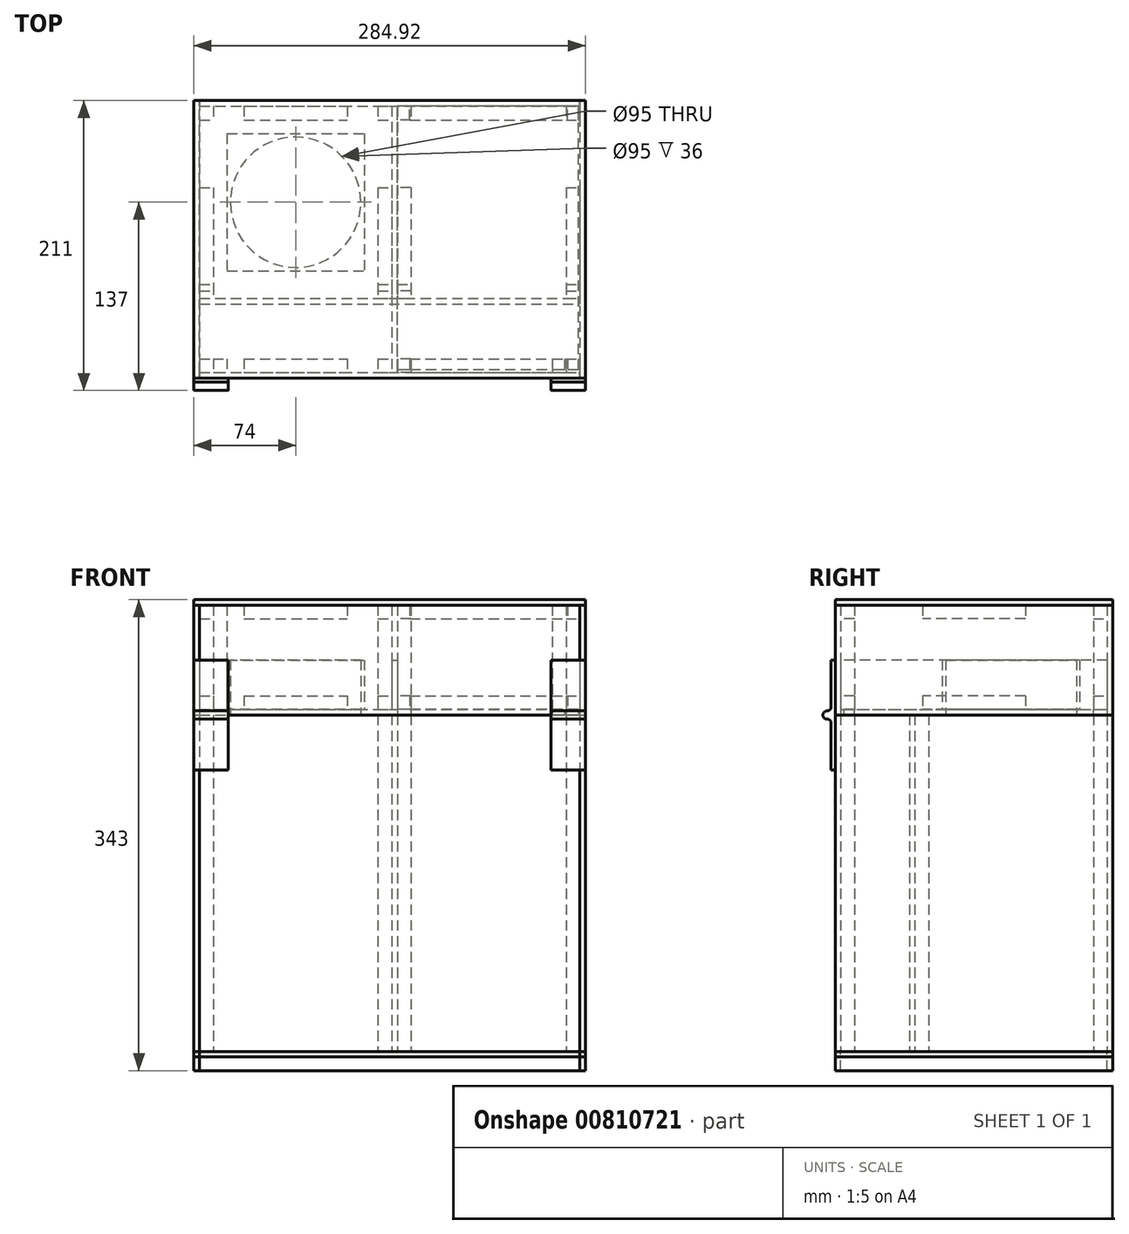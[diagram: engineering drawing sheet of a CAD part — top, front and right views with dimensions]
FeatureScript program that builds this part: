
annotation { "Feature Type Name" : "Feature", "Feature Type Description" : "" }
export const myFeature = defineFeature(function(context is Context, id is Id, definition is map)
    precondition{}
    {
        {
            assignVariable(context, id + "F0", {"name" : "Hoogte", "anyValue" : 245 * mm});
        }
        {
            assignVariable(context, id + "F1", {"name" : "Dikte", "anyValue" : 4 * mm});
        }
        {
            assignVariable(context, id + "F2", {"name" : "Hoogtedak", "anyValue" : 80 * mm});
        }
        {
            var Q0;
            Q0=qCreatedBy(makeId("Top.planeOp"),FACE);
            var sketch = newSketch(context, id + "F3", { "sketchPlane" : qUnion([Q0])});
            skPoint(sketch, "E0.second.point", {"position": v(-37.5, 0) * mm});
            skPoint(sketch, "E0.third.point", {"position": v(-144, 71.58) * mm});
            skLineSegment(sketch, "E1.bottom", {"start": v(132.92, 0) * mm, "end": v(-144, 0) * mm, "construction": true});
            skLineSegment(sketch, "E1.top", {"start": v(132.92, -4) * mm, "end": v(-144, -4) * mm, "construction": true});
            skLineSegment(sketch, "E1.left", {"start": v(132.92, 0) * mm, "end": v(132.92, -4) * mm, "construction": true});
            skLineSegment(sketch, "E1.right", {"start": v(-144, 0) * mm, "end": v(-144, -4) * mm, "construction": true});
            skCircle(sketch, "E2", {"center": v(40, 40) * mm, "radius": 40 * mm, "construction": true});
            skPoint(sketch, "E2.first.point", {"position": v(40, 0) * mm});
            skPoint(sketch, "E2.second.point", {"position": v(0, 40) * mm});
            skPoint(sketch, "E2.third.point", {"position": v(57.46, 76) * mm});
            skCircle(sketch, "E3", {"center": v(92.92, 100) * mm, "radius": 40 * mm, "construction": true});
            skPoint(sketch, "E3.first.point", {"position": v(66.46, 70) * mm});
            skPoint(sketch, "E3.second.point", {"position": v(132.92, 100) * mm});
            skPoint(sketch, "E3.third.point", {"position": v(61.07, 124.2) * mm});
            skLineSegment(sketch, "E4.bottom", {"start": v(0, 0) * mm, "end": v(-4, 0) * mm, "construction": true});
            skLineSegment(sketch, "E4.top", {"start": v(0, 140) * mm, "end": v(-4, 140) * mm, "construction": true});
            skLineSegment(sketch, "E4.left", {"start": v(0, 0) * mm, "end": v(0, 140) * mm, "construction": true});
            skLineSegment(sketch, "E4.right", {"start": v(-4, 0) * mm, "end": v(-4, 140) * mm, "construction": true});
            skCircle(sketch, "E5", {"center": v(-74, 70) * mm, "radius": 70 * mm, "construction": true});
            skPoint(sketch, "E5.first.point", {"position": v(-74, 0) * mm});
            skPoint(sketch, "E5.second.point", {"position": v(-4, 70) * mm});
            skPoint(sketch, "E5.third.point", {"position": v(-109.65, 130.24) * mm});
            skLineSegment(sketch, "E6.bottom", {"start": v(-144, -4) * mm, "end": v(132.92, -4) * mm, "construction": true});
            skLineSegment(sketch, "E6.top", {"start": v(-144, -54) * mm, "end": v(132.92, -54) * mm, "construction": true});
            skLineSegment(sketch, "E6.left", {"start": v(-144, -4) * mm, "end": v(-144, -54) * mm, "construction": true});
            skLineSegment(sketch, "E6.right", {"start": v(132.92, -4) * mm, "end": v(132.92, -54) * mm, "construction": true});
            skLineSegment(sketch, "E7.top", {"start": v(-144, 140) * mm, "end": v(132.92, 140) * mm, "construction": true});
            skLineSegment(sketch, "E7.left", {"start": v(-144, -54) * mm, "end": v(-144, 140) * mm, "construction": true});
            skLineSegment(sketch, "E7.right", {"start": v(132.92, -54) * mm, "end": v(132.92, 140) * mm, "construction": true});
            skLineSegment(sketch, "E8.bottom", {"start": v(132.92, 140) * mm, "end": v(122.92, 140) * mm, "construction": true});
            skLineSegment(sketch, "E8.top", {"start": v(132.92, 130) * mm, "end": v(122.92, 130) * mm, "construction": true});
            skLineSegment(sketch, "E8.left", {"start": v(132.92, 140) * mm, "end": v(132.92, 130) * mm, "construction": true});
            skLineSegment(sketch, "E8.right", {"start": v(122.92, 140) * mm, "end": v(122.92, 130) * mm, "construction": true});
            skLineSegment(sketch, "E9.bottom", {"start": v(0, 140) * mm, "end": v(10, 140) * mm, "construction": true});
            skLineSegment(sketch, "E9.top", {"start": v(0, 130) * mm, "end": v(10, 130) * mm, "construction": true});
            skLineSegment(sketch, "E9.left", {"start": v(0, 140) * mm, "end": v(0, 130) * mm, "construction": true});
            skLineSegment(sketch, "E9.right", {"start": v(10, 140) * mm, "end": v(10, 130) * mm, "construction": true});
            skLineSegment(sketch, "E10.bottom", {"start": v(-4, 140) * mm, "end": v(-14, 140) * mm, "construction": true});
            skLineSegment(sketch, "E10.top", {"start": v(-4, 130) * mm, "end": v(-14, 130) * mm, "construction": true});
            skLineSegment(sketch, "E10.left", {"start": v(-4, 140) * mm, "end": v(-4, 130) * mm, "construction": true});
            skLineSegment(sketch, "E10.right", {"start": v(-14, 140) * mm, "end": v(-14, 130) * mm, "construction": true});
            skLineSegment(sketch, "E11.bottom", {"start": v(-144, 140) * mm, "end": v(-134, 140) * mm, "construction": true});
            skLineSegment(sketch, "E11.top", {"start": v(-144, 130) * mm, "end": v(-134, 130) * mm, "construction": true});
            skLineSegment(sketch, "E11.left", {"start": v(-144, 140) * mm, "end": v(-144, 130) * mm, "construction": true});
            skLineSegment(sketch, "E11.right", {"start": v(-134, 140) * mm, "end": v(-134, 130) * mm, "construction": true});
            skLineSegment(sketch, "E12.bottom", {"start": v(-144, 0) * mm, "end": v(-134, 0) * mm, "construction": true});
            skLineSegment(sketch, "E12.top", {"start": v(-144, 10) * mm, "end": v(-134, 10) * mm, "construction": true});
            skLineSegment(sketch, "E12.left", {"start": v(-144, 0) * mm, "end": v(-144, 10) * mm, "construction": true});
            skLineSegment(sketch, "E12.right", {"start": v(-134, 0) * mm, "end": v(-134, 10) * mm, "construction": true});
            skLineSegment(sketch, "E13.bottom", {"start": v(-4, 0) * mm, "end": v(-14, 0) * mm, "construction": true});
            skLineSegment(sketch, "E13.top", {"start": v(-4, 10) * mm, "end": v(-14, 10) * mm, "construction": true});
            skLineSegment(sketch, "E13.left", {"start": v(-4, 0) * mm, "end": v(-4, 10) * mm, "construction": true});
            skLineSegment(sketch, "E13.right", {"start": v(-14, 0) * mm, "end": v(-14, 10) * mm, "construction": true});
            skLineSegment(sketch, "E14.bottom", {"start": v(0, 0) * mm, "end": v(10, 0) * mm, "construction": true});
            skLineSegment(sketch, "E14.top", {"start": v(0, 10) * mm, "end": v(10, 10) * mm, "construction": true});
            skLineSegment(sketch, "E14.left", {"start": v(0, 0) * mm, "end": v(0, 10) * mm, "construction": true});
            skLineSegment(sketch, "E14.right", {"start": v(10, 0) * mm, "end": v(10, 10) * mm, "construction": true});
            skLineSegment(sketch, "E15.bottom", {"start": v(132.92, 0) * mm, "end": v(122.92, 0) * mm, "construction": true});
            skLineSegment(sketch, "E15.top", {"start": v(132.92, 10) * mm, "end": v(122.92, 10) * mm, "construction": true});
            skLineSegment(sketch, "E15.left", {"start": v(132.92, 0) * mm, "end": v(132.92, 10) * mm, "construction": true});
            skLineSegment(sketch, "E15.right", {"start": v(122.92, 0) * mm, "end": v(122.92, 10) * mm, "construction": true});
            skLineSegment(sketch, "E16.bottom", {"start": v(132.92, -54) * mm, "end": v(122.92, -54) * mm, "construction": true});
            skLineSegment(sketch, "E16.top", {"start": v(132.92, -44) * mm, "end": v(122.92, -44) * mm, "construction": true});
            skLineSegment(sketch, "E16.left", {"start": v(132.92, -54) * mm, "end": v(132.92, -44) * mm, "construction": true});
            skLineSegment(sketch, "E16.right", {"start": v(122.92, -54) * mm, "end": v(122.92, -44) * mm, "construction": true});
            skLineSegment(sketch, "E17.bottom", {"start": v(-144, -54) * mm, "end": v(-134, -54) * mm, "construction": true});
            skLineSegment(sketch, "E17.top", {"start": v(-144, -44) * mm, "end": v(-134, -44) * mm, "construction": true});
            skLineSegment(sketch, "E17.left", {"start": v(-144, -54) * mm, "end": v(-144, -44) * mm, "construction": true});
            skLineSegment(sketch, "E17.right", {"start": v(-134, -54) * mm, "end": v(-134, -44) * mm, "construction": true});
            skSolve(sketch);
        }
        {
            var Q0;
            Q0=qCreatedBy(makeId("Top.planeOp"),FACE);
            var sketch = newSketch(context, id + "F4", { "sketchPlane" : qUnion([Q0])});
            skLineSegment(sketch, "E18.bottom", {"start": v(-144, 140) * mm, "end": v(-134, 140) * mm});
            skLineSegment(sketch, "E18.top", {"start": v(-144, 130) * mm, "end": v(-134, 130) * mm});
            skLineSegment(sketch, "E18.left", {"start": v(-144, 140) * mm, "end": v(-144, 130) * mm});
            skLineSegment(sketch, "E18.right", {"start": v(-134, 140) * mm, "end": v(-134, 130) * mm});
            skLineSegment(sketch, "E19.bottom", {"start": v(-14, 140) * mm, "end": v(-4, 140) * mm});
            skLineSegment(sketch, "E19.top", {"start": v(-14, 130) * mm, "end": v(-4, 130) * mm});
            skLineSegment(sketch, "E19.left", {"start": v(-14, 140) * mm, "end": v(-14, 130) * mm});
            skLineSegment(sketch, "E19.right", {"start": v(-4, 140) * mm, "end": v(-4, 130) * mm});
            skLineSegment(sketch, "E20.bottom", {"start": v(10, 140) * mm, "end": v(0, 140) * mm});
            skLineSegment(sketch, "E20.top", {"start": v(10, 130) * mm, "end": v(0, 130) * mm});
            skLineSegment(sketch, "E20.left", {"start": v(10, 140) * mm, "end": v(10, 130) * mm});
            skLineSegment(sketch, "E20.right", {"start": v(0, 140) * mm, "end": v(0, 130) * mm});
            skLineSegment(sketch, "E21.bottom", {"start": v(122.92, 140) * mm, "end": v(132.92, 140) * mm});
            skLineSegment(sketch, "E21.top", {"start": v(122.92, 130) * mm, "end": v(132.92, 130) * mm});
            skLineSegment(sketch, "E21.left", {"start": v(122.92, 140) * mm, "end": v(122.92, 130) * mm});
            skLineSegment(sketch, "E21.right", {"start": v(132.92, 140) * mm, "end": v(132.92, 130) * mm});
            skLineSegment(sketch, "E22.bottom", {"start": v(122.92, 10) * mm, "end": v(132.92, 10) * mm});
            skLineSegment(sketch, "E22.top", {"start": v(122.92, 0) * mm, "end": v(132.92, 0) * mm});
            skLineSegment(sketch, "E22.left", {"start": v(122.92, 10) * mm, "end": v(122.92, 0) * mm});
            skLineSegment(sketch, "E22.right", {"start": v(132.92, 10) * mm, "end": v(132.92, 0) * mm});
            skLineSegment(sketch, "E23.bottom", {"start": v(122.92, -44) * mm, "end": v(132.92, -44) * mm});
            skLineSegment(sketch, "E23.top", {"start": v(122.92, -54) * mm, "end": v(132.92, -54) * mm});
            skLineSegment(sketch, "E23.left", {"start": v(122.92, -44) * mm, "end": v(122.92, -54) * mm});
            skLineSegment(sketch, "E23.right", {"start": v(132.92, -44) * mm, "end": v(132.92, -54) * mm});
            skLineSegment(sketch, "E24.bottom", {"start": v(0, 10) * mm, "end": v(10, 10) * mm});
            skLineSegment(sketch, "E24.top", {"start": v(0, 0) * mm, "end": v(10, 0) * mm});
            skLineSegment(sketch, "E24.left", {"start": v(0, 10) * mm, "end": v(0, 0) * mm});
            skLineSegment(sketch, "E24.right", {"start": v(10, 10) * mm, "end": v(10, 0) * mm});
            skLineSegment(sketch, "E25.bottom", {"start": v(-14, 10) * mm, "end": v(-4, 10) * mm});
            skLineSegment(sketch, "E25.top", {"start": v(-14, 0) * mm, "end": v(-4, 0) * mm});
            skLineSegment(sketch, "E25.left", {"start": v(-14, 10) * mm, "end": v(-14, 0) * mm});
            skLineSegment(sketch, "E25.right", {"start": v(-4, 10) * mm, "end": v(-4, 0) * mm});
            skLineSegment(sketch, "E26.bottom", {"start": v(-144, 10) * mm, "end": v(-134, 10) * mm});
            skLineSegment(sketch, "E26.top", {"start": v(-144, 0) * mm, "end": v(-134, 0) * mm});
            skLineSegment(sketch, "E26.left", {"start": v(-144, 10) * mm, "end": v(-144, 0) * mm});
            skLineSegment(sketch, "E26.right", {"start": v(-134, 10) * mm, "end": v(-134, 0) * mm});
            skLineSegment(sketch, "E27.bottom", {"start": v(-144, -44) * mm, "end": v(-134, -44) * mm});
            skLineSegment(sketch, "E27.top", {"start": v(-144, -54) * mm, "end": v(-134, -54) * mm});
            skLineSegment(sketch, "E27.left", {"start": v(-144, -44) * mm, "end": v(-144, -54) * mm});
            skLineSegment(sketch, "E27.right", {"start": v(-134, -44) * mm, "end": v(-134, -54) * mm});
            skSolve(sketch);
        }
        {
            var Q0;
            Q0 = qSketchRegion(id + "F4", true);
            extrude(context, id + "F5", {"entities" : qUnion([Q0]), "depth" : getVariable(context, 'Hoogte'), "offsetDistance" : 25 * mm});
        }
        {
            var Q0;
            Q0=qCreatedBy(makeId("Top.planeOp"),FACE);
            var sketch = newSketch(context, id + "F6", { "sketchPlane" : qUnion([Q0])});
            skLineSegment(sketch, "E28.bottom", {"start": v(-144, 140) * mm, "end": v(132.92, 140) * mm});
            skLineSegment(sketch, "E28.top", {"start": v(-144, 144) * mm, "end": v(132.92, 144) * mm});
            skLineSegment(sketch, "E28.left", {"start": v(-144, 140) * mm, "end": v(-144, 144) * mm});
            skLineSegment(sketch, "E28.right", {"start": v(132.92, 140) * mm, "end": v(132.92, 144) * mm});
            skLineSegment(sketch, "E29.bottom", {"start": v(-144, 0) * mm, "end": v(132.92, 0) * mm});
            skLineSegment(sketch, "E29.top", {"start": v(-144, -4) * mm, "end": v(132.92, -4) * mm});
            skLineSegment(sketch, "E29.left", {"start": v(-144, 0) * mm, "end": v(-144, -4) * mm});
            skLineSegment(sketch, "E29.right", {"start": v(132.92, 0) * mm, "end": v(132.92, -4) * mm});
            skLineSegment(sketch, "E30.bottom", {"start": v(-144, -58) * mm, "end": v(132.92, -58) * mm});
            skLineSegment(sketch, "E30.top", {"start": v(-144, -54) * mm, "end": v(132.92, -54) * mm});
            skLineSegment(sketch, "E30.left", {"start": v(-144, -58) * mm, "end": v(-144, -54) * mm});
            skLineSegment(sketch, "E30.right", {"start": v(132.92, -58) * mm, "end": v(132.92, -54) * mm});
            skSolve(sketch);
        }
        {
            var Q0;
            Q0 = qSketchRegion(id + "F6", true);
            extrude(context, id + "F7", {"entities" : qUnion([Q0]), "depth" : getVariable(context, 'Hoogte'), "offsetDistance" : 25 * mm});
        }
        {
            var Q0;
            Q0=qCreatedBy(makeId("Top.planeOp"),FACE);
            var sketch = newSketch(context, id + "F8", { "sketchPlane" : qUnion([Q0])});
            skLineSegment(sketch, "E31.bottom", {"start": v(-148, 144) * mm, "end": v(-144, 144) * mm});
            skLineSegment(sketch, "E31.top", {"start": v(-148, -58) * mm, "end": v(-144, -58) * mm});
            skLineSegment(sketch, "E31.left", {"start": v(-148, 144) * mm, "end": v(-148, -58) * mm});
            skLineSegment(sketch, "E31.right", {"start": v(-144, 144) * mm, "end": v(-144, -58) * mm});
            skLineSegment(sketch, "E32.bottom", {"start": v(-4, 140) * mm, "end": v(0, 140) * mm});
            skLineSegment(sketch, "E32.top", {"start": v(-4, 0) * mm, "end": v(0, 0) * mm});
            skLineSegment(sketch, "E32.left", {"start": v(-4, 140) * mm, "end": v(-4, 0) * mm});
            skLineSegment(sketch, "E32.right", {"start": v(0, 140) * mm, "end": v(0, 0) * mm});
            skLineSegment(sketch, "E33.bottom", {"start": v(132.92, 144) * mm, "end": v(136.92, 144) * mm});
            skLineSegment(sketch, "E33.top", {"start": v(132.92, -58) * mm, "end": v(136.92, -58) * mm});
            skLineSegment(sketch, "E33.left", {"start": v(132.92, 144) * mm, "end": v(132.92, -58) * mm});
            skLineSegment(sketch, "E33.right", {"start": v(136.92, 144) * mm, "end": v(136.92, -58) * mm});
            skSolve(sketch);
        }
        {
            var Q0;
            Q0 = qSketchRegion(id + "F8", true);
            extrude(context, id + "F9", {"entities" : qUnion([Q0]), "depth" : getVariable(context, 'Hoogte'), "offsetDistance" : 25 * mm});
        }
        {
            var Q0;
            Q0=qCreatedBy(makeId("Top.planeOp"),FACE);
            var sketch = newSketch(context, id + "F10", { "sketchPlane" : qUnion([Q0])});
            skLineSegment(sketch, "E34.bottom", {"start": v(-148, 144) * mm, "end": v(136.92, 144) * mm});
            skLineSegment(sketch, "E34.top", {"start": v(-148, -58) * mm, "end": v(136.92, -58) * mm});
            skLineSegment(sketch, "E34.left", {"start": v(-148, 144) * mm, "end": v(-148, -58) * mm});
            skLineSegment(sketch, "E34.right", {"start": v(136.92, 144) * mm, "end": v(136.92, -58) * mm});
            skSolve(sketch);
        }
        {
            var Q0;
            Q0 = qSketchRegion(id + "F10", true);
            extrude(context, id + "F11", {"entities" : qUnion([Q0]), "oppositeDirection" : true, "depth" : getVariable(context, 'Dikte'), "offsetDistance" : 25 * mm});
        }
        {
            var Q0;
            Q0 = qSketchRegion(id + "F4", true);
            extrude(context, id + "F12", {"entities" : qUnion([Q0]), "depth" : getVariable(context, 'Hoogtedak'), "offsetDistance" : 25 * mm});
        }
        {
            var Q0;
            Q0=makeQuery(id+"F12.opExtrude","SWEPT_BODY",BODY,{"disambiguationData":[OSD([sQuery(id+"F4.wireOp",EDGE,"E27.bottom"),sQuery(id+"F4.wireOp",EDGE,"E27.top"),sQuery(id+"F4.wireOp",EDGE,"E27.left"),sQuery(id+"F4.wireOp",EDGE,"E27.right")])]});
            var Q1;
            Q1=makeQuery(id+"F12.opExtrude","SWEPT_BODY",BODY,{"disambiguationData":[OSD([sQuery(id+"F4.wireOp",EDGE,"E26.bottom"),sQuery(id+"F4.wireOp",EDGE,"E26.top"),sQuery(id+"F4.wireOp",EDGE,"E26.left"),sQuery(id+"F4.wireOp",EDGE,"E26.right")])]});
            var Q2;
            Q2=makeQuery(id+"F12.opExtrude","SWEPT_BODY",BODY,{"disambiguationData":[OSD([sQuery(id+"F4.wireOp",EDGE,"E25.bottom"),sQuery(id+"F4.wireOp",EDGE,"E25.top"),sQuery(id+"F4.wireOp",EDGE,"E25.left"),sQuery(id+"F4.wireOp",EDGE,"E25.right")])]});
            var Q3;
            Q3=makeQuery(id+"F12.opExtrude","SWEPT_BODY",BODY,{"disambiguationData":[OSD([sQuery(id+"F4.wireOp",EDGE,"E24.bottom"),sQuery(id+"F4.wireOp",EDGE,"E24.top"),sQuery(id+"F4.wireOp",EDGE,"E24.left"),sQuery(id+"F4.wireOp",EDGE,"E24.right")])]});
            var Q4;
            Q4=makeQuery(id+"F12.opExtrude","SWEPT_BODY",BODY,{"disambiguationData":[OSD([sQuery(id+"F4.wireOp",EDGE,"E23.bottom"),sQuery(id+"F4.wireOp",EDGE,"E23.top"),sQuery(id+"F4.wireOp",EDGE,"E23.left"),sQuery(id+"F4.wireOp",EDGE,"E23.right")])]});
            var Q5;
            Q5=makeQuery(id+"F12.opExtrude","SWEPT_BODY",BODY,{"disambiguationData":[OSD([sQuery(id+"F4.wireOp",EDGE,"E22.bottom"),sQuery(id+"F4.wireOp",EDGE,"E22.top"),sQuery(id+"F4.wireOp",EDGE,"E22.left"),sQuery(id+"F4.wireOp",EDGE,"E22.right")])]});
            var Q6;
            Q6=makeQuery(id+"F12.opExtrude","SWEPT_BODY",BODY,{"disambiguationData":[OSD([sQuery(id+"F4.wireOp",EDGE,"E21.bottom"),sQuery(id+"F4.wireOp",EDGE,"E21.top"),sQuery(id+"F4.wireOp",EDGE,"E21.left"),sQuery(id+"F4.wireOp",EDGE,"E21.right")])]});
            var Q7;
            Q7=makeQuery(id+"F12.opExtrude","SWEPT_BODY",BODY,{"disambiguationData":[OSD([sQuery(id+"F4.wireOp",EDGE,"E20.bottom"),sQuery(id+"F4.wireOp",EDGE,"E20.top"),sQuery(id+"F4.wireOp",EDGE,"E20.left"),sQuery(id+"F4.wireOp",EDGE,"E20.right")])]});
            var Q8;
            Q8=makeQuery(id+"F12.opExtrude","SWEPT_BODY",BODY,{"disambiguationData":[OSD([sQuery(id+"F4.wireOp",EDGE,"E19.bottom"),sQuery(id+"F4.wireOp",EDGE,"E19.top"),sQuery(id+"F4.wireOp",EDGE,"E19.left"),sQuery(id+"F4.wireOp",EDGE,"E19.right")])]});
            var Q9;
            Q9=makeQuery(id+"F12.opExtrude","SWEPT_BODY",BODY,{"disambiguationData":[OSD([sQuery(id+"F4.wireOp",EDGE,"E18.bottom"),sQuery(id+"F4.wireOp",EDGE,"E18.top"),sQuery(id+"F4.wireOp",EDGE,"E18.left"),sQuery(id+"F4.wireOp",EDGE,"E18.right")])]});
            transform(context, id + "F13", {"entities" : qUnion([Q0, Q1, Q2, Q3, Q4, Q5, Q6, Q7, Q8, Q9]), "transformType" : TransformType.TRANSLATION_3D, "dx" : 0 * mm, "dy" : 0 * mm, "dz" : getVariable(context, 'Hoogte'), "makeCopy" : false});
        }
        {
            var Q0;
            Q0=qCreatedBy(makeId("Top.planeOp"),FACE);
            cPlane(context, id + "F14", {"entities" : qUnion([Q0]), "cplaneType" : CPlaneType.OFFSET, "offset" : getVariable(context, 'Hoogte'), "width" : 150 * mm, "height" : 150 * mm});
        }
        {
            var Q0;
            Q0=qCreatedBy(id+"F14.planeOp",FACE);
            var sketch = newSketch(context, id + "F15", { "sketchPlane" : qUnion([Q0])});
            skLineSegment(sketch, "E35.bottom", {"start": v(-144, -58) * mm, "end": v(132.92, -58) * mm});
            skLineSegment(sketch, "E35.top", {"start": v(-144, -54) * mm, "end": v(132.92, -54) * mm});
            skLineSegment(sketch, "E35.left", {"start": v(-144, -58) * mm, "end": v(-144, -54) * mm});
            skLineSegment(sketch, "E35.right", {"start": v(132.92, -58) * mm, "end": v(132.92, -54) * mm});
            skLineSegment(sketch, "E36.bottom", {"start": v(-144, 144) * mm, "end": v(132.92, 144) * mm});
            skLineSegment(sketch, "E36.top", {"start": v(-144, 140) * mm, "end": v(132.92, 140) * mm});
            skLineSegment(sketch, "E36.left", {"start": v(-144, 144) * mm, "end": v(-144, 140) * mm});
            skLineSegment(sketch, "E36.right", {"start": v(132.92, 144) * mm, "end": v(132.92, 140) * mm});
            skSolve(sketch);
        }
        {
            var Q0;
            Q0=qCreatedBy(id+"F14.planeOp",FACE);
            var sketch = newSketch(context, id + "F16", { "sketchPlane" : qUnion([Q0])});
            skLineSegment(sketch, "E37.bottom", {"start": v(-148, 144) * mm, "end": v(-144, 144) * mm});
            skLineSegment(sketch, "E37.top", {"start": v(-148, -58) * mm, "end": v(-144, -58) * mm});
            skLineSegment(sketch, "E37.left", {"start": v(-148, 144) * mm, "end": v(-148, -58) * mm});
            skLineSegment(sketch, "E37.right", {"start": v(-144, 144) * mm, "end": v(-144, -58) * mm});
            skLineSegment(sketch, "E38.bottom", {"start": v(132.92, 144) * mm, "end": v(136.92, 144) * mm});
            skLineSegment(sketch, "E38.top", {"start": v(132.92, -58) * mm, "end": v(136.92, -58) * mm});
            skLineSegment(sketch, "E38.left", {"start": v(132.92, 144) * mm, "end": v(132.92, -58) * mm});
            skLineSegment(sketch, "E38.right", {"start": v(136.92, 144) * mm, "end": v(136.92, -58) * mm});
            skSolve(sketch);
        }
        {
            var Q0;
            Q0 = qSketchRegion(id + "F15", true);
            var Q1;
            Q1 = qSketchRegion(id + "F16", true);
            extrude(context, id + "F17", {"entities" : qUnion([Q0, Q1]), "depth" : getVariable(context, 'Hoogtedak'), "offsetDistance" : 25 * mm});
        }
        {
            var Q0;
            Q0=qCreatedBy(id+"F14.planeOp",FACE);
            cPlane(context, id + "F18", {"entities" : qUnion([Q0]), "cplaneType" : CPlaneType.OFFSET, "offset" : getVariable(context, 'Hoogtedak'), "width" : 150 * mm, "height" : 150 * mm});
        }
        {
            var Q0;
            Q0=qCreatedBy(id+"F18.planeOp",FACE);
            var sketch = newSketch(context, id + "F19", { "sketchPlane" : qUnion([Q0])});
            skLineSegment(sketch, "E39.bottom", {"start": v(-148, 144) * mm, "end": v(136.92, 144) * mm});
            skLineSegment(sketch, "E39.top", {"start": v(-148, -58) * mm, "end": v(136.92, -58) * mm});
            skLineSegment(sketch, "E39.left", {"start": v(-148, 144) * mm, "end": v(-148, -58) * mm});
            skLineSegment(sketch, "E39.right", {"start": v(136.92, 144) * mm, "end": v(136.92, -58) * mm});
            skSolve(sketch);
        }
        {
            var Q0;
            Q0 = qSketchRegion(id + "F19", true);
            extrude(context, id + "F20", {"entities" : qUnion([Q0]), "depth" : getVariable(context, 'Dikte'), "offsetDistance" : 25 * mm});
        }
        {
            var Q0;
            Q0=makeQuery(id+"F12.opExtrude","SWEPT_BODY",BODY,{"disambiguationData":[OSD([sQuery(id+"F4.wireOp",EDGE,"E24.bottom"),sQuery(id+"F4.wireOp",EDGE,"E24.top"),sQuery(id+"F4.wireOp",EDGE,"E24.left"),sQuery(id+"F4.wireOp",EDGE,"E24.right")])]});
            var Q1;
            Q1=makeQuery(id+"F12.opExtrude","SWEPT_BODY",BODY,{"disambiguationData":[OSD([sQuery(id+"F4.wireOp",EDGE,"E25.bottom"),sQuery(id+"F4.wireOp",EDGE,"E25.top"),sQuery(id+"F4.wireOp",EDGE,"E25.left"),sQuery(id+"F4.wireOp",EDGE,"E25.right")])]});
            var Q2;
            Q2=makeQuery(id+"F12.opExtrude","SWEPT_BODY",BODY,{"disambiguationData":[OSD([sQuery(id+"F4.wireOp",EDGE,"E22.bottom"),sQuery(id+"F4.wireOp",EDGE,"E22.top"),sQuery(id+"F4.wireOp",EDGE,"E22.left"),sQuery(id+"F4.wireOp",EDGE,"E22.right")])]});
            deleteBodies(context, id + "F21", {"entities" : qUnion([Q0, Q1, Q2])});
        }
        {
            var Q0;
            Q0=makeQuery(id+"F12.opExtrude","SWEPT_BODY",BODY,{"disambiguationData":[OSD([sQuery(id+"F4.wireOp",EDGE,"E26.bottom"),sQuery(id+"F4.wireOp",EDGE,"E26.top"),sQuery(id+"F4.wireOp",EDGE,"E26.left"),sQuery(id+"F4.wireOp",EDGE,"E26.right")])]});
            deleteBodies(context, id + "F22", {"entities" : qUnion([Q0])});
        }
        {
            var Q0;
            Q0=makeQuery(id+"F12.opExtrude","SWEPT_BODY",BODY,{"disambiguationData":[OSD([sQuery(id+"F4.wireOp",EDGE,"E19.bottom"),sQuery(id+"F4.wireOp",EDGE,"E19.top"),sQuery(id+"F4.wireOp",EDGE,"E19.left"),sQuery(id+"F4.wireOp",EDGE,"E19.right")])]});
            var Q1;
            Q1=makeQuery(id+"F12.opExtrude","SWEPT_BODY",BODY,{"disambiguationData":[OSD([sQuery(id+"F4.wireOp",EDGE,"E20.bottom"),sQuery(id+"F4.wireOp",EDGE,"E20.top"),sQuery(id+"F4.wireOp",EDGE,"E20.left"),sQuery(id+"F4.wireOp",EDGE,"E20.right")])]});
            var Q2;
            Q2=sQuery(id+"F3.wireOp",VERTEX,"E7.top.end");
            var Q3;
            Q3=sQuery(id+"F3.wireOp",VERTEX,"E16.top.start");
            transform(context, id + "F23", {"entities" : qUnion([Q0, Q1]), "transformType" : TransformType.TRANSLATION_ENTITY, "oppositeDirectionEntity" : false, "transformLine" : qUnion([Q2, Q3]), "makeCopy" : true});
        }
        {
            var Q0;
            Q0=qCreatedBy(id+"F14.planeOp",FACE);
            var sketch = newSketch(context, id + "F24", { "sketchPlane" : qUnion([Q0])});
            skLineSegment(sketch, "E40.bottom", {"start": v(-4, 140) * mm, "end": v(0, 140) * mm});
            skLineSegment(sketch, "E40.top", {"start": v(-4, -54) * mm, "end": v(0, -54) * mm});
            skLineSegment(sketch, "E40.left", {"start": v(-4, 140) * mm, "end": v(-4, -54) * mm});
            skLineSegment(sketch, "E40.right", {"start": v(0, 140) * mm, "end": v(0, -54) * mm});
            skLineSegment(sketch, "E41.bottom", {"start": v(-124, 120) * mm, "end": v(-24, 120) * mm});
            skLineSegment(sketch, "E41.top", {"start": v(-124, 20) * mm, "end": v(-24, 20) * mm});
            skLineSegment(sketch, "E41.left", {"start": v(-124, 120) * mm, "end": v(-124, 20) * mm});
            skLineSegment(sketch, "E41.right", {"start": v(-24, 120) * mm, "end": v(-24, 20) * mm});
            skLineSegment(sketch, "E42", {"start": v(-74, 20) * mm, "end": v(-74, 120) * mm, "construction": true});
            skPoint(sketch, "E42.startSnap0", {"position": v(-74, 20) * mm});
            skLineSegment(sketch, "E43", {"start": v(-124, 70) * mm, "end": v(-24, 70) * mm, "construction": true});
            skSolve(sketch);
        }
        {
            var Q0;
            Q0 = qSketchRegion(id + "F24", true);
            extrude(context, id + "F25", {"entities" : qUnion([Q0]), "depth" : getVariable(context, 'Hoogtedak') / 2, "offsetDistance" : 25 * mm});
        }
        {
            var Q0;
            Q0=qCreatedBy(id+"F14.planeOp",FACE);
            var sketch = newSketch(context, id + "F26", { "sketchPlane" : qUnion([Q0])});
            skLineSegment(sketch, "E44.bottom", {"start": v(-144, -54) * mm, "end": v(0, -54) * mm});
            skLineSegment(sketch, "E44.top", {"start": v(-144, 140) * mm, "end": v(0, 140) * mm});
            skLineSegment(sketch, "E44.left", {"start": v(-144, -54) * mm, "end": v(-144, 140) * mm});
            skLineSegment(sketch, "E44.right", {"start": v(0, -54) * mm, "end": v(0, 140) * mm});
            skSolve(sketch);
        }
        {
            var Q0;
            Q0 = qSketchRegion(id + "F26", true);
            extrude(context, id + "F27", {"entities" : qUnion([Q0]), "depth" : getVariable(context, 'Dikte'), "offsetDistance" : 25 * mm});
        }
        {
            var Q0;
            Q0=makeQuery(id+"F27.opExtrude","SWEPT_BODY",BODY,{"disambiguationData":[OSD([sQuery(id+"F26.wireOp",EDGE,"E44.bottom"),sQuery(id+"F26.wireOp",EDGE,"E44.top"),sQuery(id+"F26.wireOp",EDGE,"E44.left"),sQuery(id+"F26.wireOp",EDGE,"E44.right")])]});
            var Q1;
            Q1=makeQuery(id+"F25.opExtrude","SWEPT_BODY",BODY,{"disambiguationData":[OSD([sQuery(id+"F24.wireOp",EDGE,"E40.bottom"),sQuery(id+"F24.wireOp",EDGE,"E40.top"),sQuery(id+"F24.wireOp",EDGE,"E40.left"),sQuery(id+"F24.wireOp",EDGE,"E40.right")])]});
            var Q2;
            Q2=makeQuery(id+"F12.opExtrude","SWEPT_BODY",BODY,{"disambiguationData":[OSD([sQuery(id+"F4.wireOp",EDGE,"E27.bottom"),sQuery(id+"F4.wireOp",EDGE,"E27.top"),sQuery(id+"F4.wireOp",EDGE,"E27.left"),sQuery(id+"F4.wireOp",EDGE,"E27.right")])]});
            var Q3;
            Q3=makeQuery(id+"F23.opPattern","COPY",BODY,{"derivedFrom":makeQuery(id+"F12.opExtrude","SWEPT_BODY",BODY,{"disambiguationData":[OSD([sQuery(id+"F4.wireOp",EDGE,"E19.bottom"),sQuery(id+"F4.wireOp",EDGE,"E19.top"),sQuery(id+"F4.wireOp",EDGE,"E19.left"),sQuery(id+"F4.wireOp",EDGE,"E19.right")])]}),"instanceName":"1"});
            var Q4;
            Q4=makeQuery(id+"F12.opExtrude","SWEPT_BODY",BODY,{"disambiguationData":[OSD([sQuery(id+"F4.wireOp",EDGE,"E18.bottom"),sQuery(id+"F4.wireOp",EDGE,"E18.top"),sQuery(id+"F4.wireOp",EDGE,"E18.left"),sQuery(id+"F4.wireOp",EDGE,"E18.right")])]});
            var Q5;
            Q5=makeQuery(id+"F12.opExtrude","SWEPT_BODY",BODY,{"disambiguationData":[OSD([sQuery(id+"F4.wireOp",EDGE,"E19.bottom"),sQuery(id+"F4.wireOp",EDGE,"E19.top"),sQuery(id+"F4.wireOp",EDGE,"E19.left"),sQuery(id+"F4.wireOp",EDGE,"E19.right")])]});
            var Q6;
            Q6=makeQuery(id+"F25.opExtrude","SWEPT_BODY",BODY,{"disambiguationData":[OSD([sQuery(id+"F24.wireOp",EDGE,"E41.bottom"),sQuery(id+"F24.wireOp",EDGE,"E41.top"),sQuery(id+"F24.wireOp",EDGE,"E41.left"),sQuery(id+"F24.wireOp",EDGE,"E41.right")])]});
            booleanBodies(context, id + "F28", {"operationType" : BooleanOperationType.SUBTRACTION, "tools" : qUnion([Q0]), "targets" : qUnion([Q1, Q2, Q3, Q4, Q5, Q6]), "keepTools" : true});
        }
        {
            var Q0;
            Q0=qCreatedBy(id+"F14.planeOp",FACE);
            var sketch = newSketch(context, id + "F29", { "sketchPlane" : qUnion([Q0])});
            skLineSegment(sketch, "E45.bottom", {"start": v(131.92, -52) * mm, "end": v(0, -52) * mm});
            skLineSegment(sketch, "E45.top", {"start": v(131.92, 140) * mm, "end": v(0, 140) * mm});
            skLineSegment(sketch, "E45.left", {"start": v(131.92, -52) * mm, "end": v(131.92, 140) * mm});
            skLineSegment(sketch, "E45.right", {"start": v(0, -52) * mm, "end": v(0, 140) * mm});
            skSolve(sketch);
        }
        {
            var Q0;
            Q0 = qSketchRegion(id + "F29", true);
            extrude(context, id + "F30", {"entities" : qUnion([Q0]), "depth" : getVariable(context, 'Dikte'), "offsetDistance" : 25 * mm});
        }
        {
            var Q0;
            Q0=makeQuery(id+"F30.opExtrude","SWEPT_BODY",BODY,{"disambiguationData":[OSD([sQuery(id+"F29.wireOp",EDGE,"E45.bottom"),sQuery(id+"F29.wireOp",EDGE,"E45.top"),sQuery(id+"F29.wireOp",EDGE,"E45.left"),sQuery(id+"F29.wireOp",EDGE,"E45.right")])]});
            var Q1;
            Q1=makeQuery(id+"F12.opExtrude","SWEPT_BODY",BODY,{"disambiguationData":[OSD([sQuery(id+"F4.wireOp",EDGE,"E21.bottom"),sQuery(id+"F4.wireOp",EDGE,"E21.top"),sQuery(id+"F4.wireOp",EDGE,"E21.left"),sQuery(id+"F4.wireOp",EDGE,"E21.right")])]});
            var Q2;
            Q2=makeQuery(id+"F12.opExtrude","SWEPT_BODY",BODY,{"disambiguationData":[OSD([sQuery(id+"F4.wireOp",EDGE,"E20.bottom"),sQuery(id+"F4.wireOp",EDGE,"E20.top"),sQuery(id+"F4.wireOp",EDGE,"E20.left"),sQuery(id+"F4.wireOp",EDGE,"E20.right")])]});
            var Q3;
            Q3=makeQuery(id+"F23.opPattern","COPY",BODY,{"derivedFrom":makeQuery(id+"F12.opExtrude","SWEPT_BODY",BODY,{"disambiguationData":[OSD([sQuery(id+"F4.wireOp",EDGE,"E20.bottom"),sQuery(id+"F4.wireOp",EDGE,"E20.top"),sQuery(id+"F4.wireOp",EDGE,"E20.left"),sQuery(id+"F4.wireOp",EDGE,"E20.right")])]}),"instanceName":"1"});
            var Q4;
            Q4=makeQuery(id+"F12.opExtrude","SWEPT_BODY",BODY,{"disambiguationData":[OSD([sQuery(id+"F4.wireOp",EDGE,"E23.bottom"),sQuery(id+"F4.wireOp",EDGE,"E23.top"),sQuery(id+"F4.wireOp",EDGE,"E23.left"),sQuery(id+"F4.wireOp",EDGE,"E23.right")])]});
            booleanBodies(context, id + "F31", {"operationType" : BooleanOperationType.SUBTRACTION, "tools" : qUnion([Q0]), "targets" : qUnion([Q1, Q2, Q3, Q4]), "keepTools" : true});
        }
        {
            var Q0;
            Q0=makeQuery(id+"F30.opExtrude","CAP_FACE",FACE,{"disambiguationData":[OSD([sQuery(id+"F29.wireOp",EDGE,"E45.bottom"),sQuery(id+"F29.wireOp",EDGE,"E45.top"),sQuery(id+"F29.wireOp",EDGE,"E45.left"),sQuery(id+"F29.wireOp",EDGE,"E45.right")])],"isStart":false});
            var sketch = newSketch(context, id + "F32", { "sketchPlane" : qUnion([Q0])});
            skLineSegment(sketch, "E46.bottom", {"start": v(9, 130) * mm, "end": v(123.92, 130) * mm});
            skLineSegment(sketch, "E46.top", {"start": v(9, 140) * mm, "end": v(123.92, 140) * mm});
            skLineSegment(sketch, "E46.left", {"start": v(9, 130) * mm, "end": v(9, 140) * mm});
            skLineSegment(sketch, "E46.right", {"start": v(123.92, 130) * mm, "end": v(123.92, 140) * mm});
            skLineSegment(sketch, "E47.bottom", {"start": v(9, -44) * mm, "end": v(123.92, -44) * mm});
            skLineSegment(sketch, "E47.top", {"start": v(9, -54) * mm, "end": v(123.92, -54) * mm});
            skLineSegment(sketch, "E47.left", {"start": v(9, -44) * mm, "end": v(9, -54) * mm});
            skLineSegment(sketch, "E47.right", {"start": v(123.92, -44) * mm, "end": v(123.92, -54) * mm});
            skLineSegment(sketch, "E48.bottom", {"start": v(-111.5, 140) * mm, "end": v(-36.5, 140) * mm});
            skLineSegment(sketch, "E48.top", {"start": v(-111.5, 130) * mm, "end": v(-36.5, 130) * mm});
            skLineSegment(sketch, "E48.left", {"start": v(-111.5, 140) * mm, "end": v(-111.5, 130) * mm});
            skLineSegment(sketch, "E48.right", {"start": v(-36.5, 140) * mm, "end": v(-36.5, 130) * mm});
            skLineSegment(sketch, "E49.bottom", {"start": v(-14, 80.5) * mm, "end": v(-4, 80.5) * mm});
            skLineSegment(sketch, "E49.top", {"start": v(-14, 5.5) * mm, "end": v(-4, 5.5) * mm});
            skLineSegment(sketch, "E49.left", {"start": v(-14, 80.5) * mm, "end": v(-14, 5.5) * mm});
            skLineSegment(sketch, "E49.right", {"start": v(-4, 80.5) * mm, "end": v(-4, 5.5) * mm});
            skLineSegment(sketch, "E50.bottom", {"start": v(10, 80.5) * mm, "end": v(0, 80.5) * mm});
            skLineSegment(sketch, "E50.top", {"start": v(10, 5.5) * mm, "end": v(0, 5.5) * mm});
            skLineSegment(sketch, "E50.left", {"start": v(10, 80.5) * mm, "end": v(10, 5.5) * mm});
            skLineSegment(sketch, "E50.right", {"start": v(0, 80.5) * mm, "end": v(0, 5.5) * mm});
            skLineSegment(sketch, "E51.bottom", {"start": v(122.92, 80.5) * mm, "end": v(132.92, 80.5) * mm});
            skLineSegment(sketch, "E51.top", {"start": v(122.92, 5.5) * mm, "end": v(132.92, 5.5) * mm});
            skLineSegment(sketch, "E51.left", {"start": v(122.92, 80.5) * mm, "end": v(122.92, 5.5) * mm});
            skLineSegment(sketch, "E51.right", {"start": v(132.92, 80.5) * mm, "end": v(132.92, 5.5) * mm});
            skLineSegment(sketch, "E52.bottom", {"start": v(-111.5, -44) * mm, "end": v(-36.5, -44) * mm});
            skLineSegment(sketch, "E52.top", {"start": v(-111.5, -54) * mm, "end": v(-36.5, -54) * mm});
            skLineSegment(sketch, "E52.left", {"start": v(-111.5, -44) * mm, "end": v(-111.5, -54) * mm});
            skLineSegment(sketch, "E52.right", {"start": v(-36.5, -44) * mm, "end": v(-36.5, -54) * mm});
            skLineSegment(sketch, "E53.bottom", {"start": v(-144, 80.5) * mm, "end": v(-134, 80.5) * mm});
            skLineSegment(sketch, "E53.top", {"start": v(-144, 5.5) * mm, "end": v(-134, 5.5) * mm});
            skLineSegment(sketch, "E53.left", {"start": v(-144, 80.5) * mm, "end": v(-144, 5.5) * mm});
            skLineSegment(sketch, "E53.right", {"start": v(-134, 80.5) * mm, "end": v(-134, 5.5) * mm});
            skLineSegment(sketch, "E54", {"start": v(-144, 140) * mm, "end": v(-4, 140) * mm, "construction": true});
            skPoint(sketch, "E55", {"position": v(-74, 140) * mm});
            skLineSegment(sketch, "E56", {"start": v(-144, 140) * mm, "end": v(-144, -54) * mm, "construction": true});
            skPoint(sketch, "E57", {"position": v(-144, 43) * mm});
            skLineSegment(sketch, "E58", {"start": v(-4, 140) * mm, "end": v(-4, -54) * mm, "construction": true});
            skLineSegment(sketch, "E59", {"start": v(-144, -54) * mm, "end": v(-4, -54) * mm, "construction": true});
            skLineSegment(sketch, "E60", {"start": v(132.92, -54) * mm, "end": v(0, -54) * mm, "construction": true});
            skLineSegment(sketch, "E61", {"start": v(0, -54) * mm, "end": v(0, 140) * mm, "construction": true});
            skLineSegment(sketch, "E62", {"start": v(0, 140) * mm, "end": v(132.92, 140) * mm, "construction": true});
            skLineSegment(sketch, "E63", {"start": v(132.92, 140) * mm, "end": v(132.92, -54) * mm, "construction": true});
            skPoint(sketch, "E64", {"position": v(0, 43) * mm});
            skPoint(sketch, "E65", {"position": v(-4, 43) * mm});
            skPoint(sketch, "E66", {"position": v(-74, -54) * mm});
            skPoint(sketch, "E67", {"position": v(66.46, -54) * mm});
            skPoint(sketch, "E68", {"position": v(132.92, 43) * mm});
            skPoint(sketch, "E69", {"position": v(66.46, 140) * mm});
            skSolve(sketch);
        }
        {
            var Q0;
            Q0 = qSketchRegion(id + "F32", true);
            extrude(context, id + "F33", {"entities" : qUnion([Q0]), "depth" : 10 * mm, "offsetDistance" : 25 * mm});
        }
        {
            var Q0;
            Q0=makeQuery(id+"F27.opExtrude","CAP_FACE",FACE,{"disambiguationData":[OSD([sQuery(id+"F26.wireOp",EDGE,"E44.bottom"),sQuery(id+"F26.wireOp",EDGE,"E44.top"),sQuery(id+"F26.wireOp",EDGE,"E44.left"),sQuery(id+"F26.wireOp",EDGE,"E44.right")])],"isStart":false});
            var sketch = newSketch(context, id + "F34", { "sketchPlane" : qUnion([Q0])});
            skCircle(sketch, "E70", {"center": v(-74, 70) * mm, "radius": 47.5 * mm});
            skSolve(sketch);
        }
        {
            var Q0;
            Q0 = qSketchRegion(id + "F34", true);
            extrude(context, id + "F35", {"entities" : qUnion([Q0]), "operationType" : NewBodyOperationType.REMOVE, "endBound" : BoundingType.SYMMETRIC, "depth" : getVariable(context, 'Hoogtedak'), "offsetDistance" : 25 * mm});
        }
        {
            var Q0;
            Q0=makeQuery(id+"F9.opExtrude","SWEPT_FACE",FACE,{"disambiguationData":[OSD([sQuery(id+"F8.wireOp",EDGE,"E33.right")])]});
            var sketch = newSketch(context, id + "F36", { "sketchPlane" : qUnion([Q0])});
            skLineSegment(sketch, "E71", {"start": v(-58, 285) * mm, "end": v(-58, 245) * mm});
            skLineSegment(sketch, "E72", {"start": v(-64, 242) * mm, "end": v(-64, 242) * mm});
            skLineSegment(sketch, "E73", {"start": v(-67, 245) * mm, "end": v(-67, 245) * mm});
            skLineSegment(sketch, "E74", {"start": v(-64, 248) * mm, "end": v(-64, 248) * mm});
            skLineSegment(sketch, "E75", {"start": v(-61, 251) * mm, "end": v(-61, 285) * mm});
            skLineSegment(sketch, "E76", {"start": v(-61, 285) * mm, "end": v(-58, 285) * mm});
            skPoint(sketch, "E77.visualSharp", {"position": v(-61, 248) * mm});
            skArc(sketch, "E77.filletArc", {"start": v(-64, 248) * mm, "mid": v(-61.88, 248.88) * mm, "end": v(-61, 251) * mm});
            skPoint(sketch, "E78.visualSharp", {"position": v(-67, 242) * mm});
            skArc(sketch, "E78.filletArc", {"start": v(-67, 245) * mm, "mid": v(-66.12, 242.88) * mm, "end": v(-64, 242) * mm});
            skPoint(sketch, "E79.visualSharp", {"position": v(-67, 248) * mm});
            skArc(sketch, "E79.filletArc", {"start": v(-64, 248) * mm, "mid": v(-66.12, 247.12) * mm, "end": v(-67, 245) * mm});
            skPoint(sketch, "E80.visualSharp", {"position": v(-58, 242) * mm});
            skLineSegment(sketch, "E81", {"start": v(-58, 245) * mm, "end": v(-58, 205) * mm});
            skLineSegment(sketch, "E82", {"start": v(-58, 205) * mm, "end": v(-61, 205) * mm});
            skLineSegment(sketch, "E83", {"start": v(-61, 205) * mm, "end": v(-61, 239) * mm});
            skPoint(sketch, "E84.visualSharp", {"position": v(-61, 242) * mm});
            skArc(sketch, "E84.filletArc", {"start": v(-61, 239) * mm, "mid": v(-61.88, 241.12) * mm, "end": v(-64, 242) * mm});
            skSolve(sketch);
        }
        {
            var Q0;
            Q0 = qSketchRegion(id + "F36", true);
            extrude(context, id + "F37", {"entities" : qUnion([Q0]), "oppositeDirection" : true, "depth" : 25 * mm, "offsetDistance" : 25 * mm});
        }
        {
            var Q0;
            Q0=makeQuery(id+"F37.opExtrude","SWEPT_BODY",BODY,{"disambiguationData":[OSD([sQuery(id+"F36.wireOp",EDGE,"E71"),sQuery(id+"F36.wireOp",EDGE,"E75"),sQuery(id+"F36.wireOp",EDGE,"E76"),sQuery(id+"F36.wireOp",EDGE,"E77.filletArc"),sQuery(id+"F36.wireOp",EDGE,"E78.filletArc"),sQuery(id+"F36.wireOp",EDGE,"E79.filletArc"),sQuery(id+"F36.wireOp",EDGE,"E81"),sQuery(id+"F36.wireOp",EDGE,"E82"),sQuery(id+"F36.wireOp",EDGE,"E83"),sQuery(id+"F36.wireOp",EDGE,"E84.filletArc")])]});
            var Q1;
            Q1=makeQuery(id+"F20.opExtrude","CAP_VERTEX",VERTEX,{"disambiguationData":[OSD([sQuery(id+"F19.wireOp",EDGE,"E39.top"),sQuery(id+"F19.wireOp",EDGE,"E39.right")])],"isStart":false});
            var Q2;
            Q2=makeQuery(id+"F20.opExtrude","CAP_VERTEX",VERTEX,{"disambiguationData":[OSD([sQuery(id+"F19.wireOp",EDGE,"E39.top"),sQuery(id+"F19.wireOp",EDGE,"E39.left")])],"isStart":false});
            transform(context, id + "F38", {"entities" : qUnion([Q0]), "transformType" : TransformType.TRANSLATION_ENTITY, "oppositeDirectionEntity" : false, "transformLine" : qUnion([Q1, Q2]), "makeCopy" : true});
        }
        {
            var Q0;
            Q0=makeQuery(id+"F38.opPattern","COPY",BODY,{"derivedFrom":makeQuery(id+"F37.opExtrude","SWEPT_BODY",BODY,{"disambiguationData":[OSD([sQuery(id+"F36.wireOp",EDGE,"E71"),sQuery(id+"F36.wireOp",EDGE,"E75"),sQuery(id+"F36.wireOp",EDGE,"E76"),sQuery(id+"F36.wireOp",EDGE,"E77.filletArc"),sQuery(id+"F36.wireOp",EDGE,"E78.filletArc"),sQuery(id+"F36.wireOp",EDGE,"E79.filletArc"),sQuery(id+"F36.wireOp",EDGE,"E81"),sQuery(id+"F36.wireOp",EDGE,"E82"),sQuery(id+"F36.wireOp",EDGE,"E83"),sQuery(id+"F36.wireOp",EDGE,"E84.filletArc")])]}),"instanceName":"1"});
            transform(context, id + "F39", {"entities" : qUnion([Q0]), "transformType" : TransformType.TRANSLATION_3D, "dx" : 25 * mm, "dy" : 0 * mm, "dz" : 0 * mm, "makeCopy" : false});
        }
        {
            var Q0;
            Q0=makeQuery(id+"F33.opExtrude","SWEPT_BODY",BODY,{"disambiguationData":[OSD([sQuery(id+"F32.wireOp",EDGE,"E46.bottom"),sQuery(id+"F32.wireOp",EDGE,"E46.top"),sQuery(id+"F32.wireOp",EDGE,"E46.left"),sQuery(id+"F32.wireOp",EDGE,"E46.right")])]});
            var Q1;
            Q1=makeQuery(id+"F33.opExtrude","SWEPT_BODY",BODY,{"disambiguationData":[OSD([sQuery(id+"F32.wireOp",EDGE,"E47.bottom"),sQuery(id+"F32.wireOp",EDGE,"E47.top"),sQuery(id+"F32.wireOp",EDGE,"E47.left"),sQuery(id+"F32.wireOp",EDGE,"E47.right")])]});
            var Q2;
            Q2=makeQuery(id+"F33.opExtrude","SWEPT_BODY",BODY,{"disambiguationData":[OSD([sQuery(id+"F32.wireOp",EDGE,"E48.bottom"),sQuery(id+"F32.wireOp",EDGE,"E48.top"),sQuery(id+"F32.wireOp",EDGE,"E48.left"),sQuery(id+"F32.wireOp",EDGE,"E48.right")])]});
            var Q3;
            Q3=makeQuery(id+"F33.opExtrude","SWEPT_BODY",BODY,{"disambiguationData":[OSD([sQuery(id+"F32.wireOp",EDGE,"E49.bottom"),sQuery(id+"F32.wireOp",EDGE,"E49.top"),sQuery(id+"F32.wireOp",EDGE,"E49.left"),sQuery(id+"F32.wireOp",EDGE,"E49.right")])]});
            var Q4;
            Q4=makeQuery(id+"F33.opExtrude","SWEPT_BODY",BODY,{"disambiguationData":[OSD([sQuery(id+"F32.wireOp",EDGE,"E50.bottom"),sQuery(id+"F32.wireOp",EDGE,"E50.top"),sQuery(id+"F32.wireOp",EDGE,"E50.left"),sQuery(id+"F32.wireOp",EDGE,"E50.right")])]});
            var Q5;
            Q5=makeQuery(id+"F33.opExtrude","SWEPT_BODY",BODY,{"disambiguationData":[OSD([sQuery(id+"F32.wireOp",EDGE,"E51.bottom"),sQuery(id+"F32.wireOp",EDGE,"E51.top"),sQuery(id+"F32.wireOp",EDGE,"E51.left"),sQuery(id+"F32.wireOp",EDGE,"E51.right")])]});
            var Q6;
            Q6=makeQuery(id+"F33.opExtrude","SWEPT_BODY",BODY,{"disambiguationData":[OSD([sQuery(id+"F32.wireOp",EDGE,"E52.bottom"),sQuery(id+"F32.wireOp",EDGE,"E52.top"),sQuery(id+"F32.wireOp",EDGE,"E52.left"),sQuery(id+"F32.wireOp",EDGE,"E52.right")])]});
            var Q7;
            Q7=makeQuery(id+"F33.opExtrude","SWEPT_BODY",BODY,{"disambiguationData":[OSD([sQuery(id+"F32.wireOp",EDGE,"E53.bottom"),sQuery(id+"F32.wireOp",EDGE,"E53.top"),sQuery(id+"F32.wireOp",EDGE,"E53.left"),sQuery(id+"F32.wireOp",EDGE,"E53.right")])]});
            transform(context, id + "F40", {"entities" : qUnion([Q0, Q1, Q2, Q3, Q4, Q5, Q6, Q7]), "transformType" : TransformType.TRANSLATION_3D, "dx" : 0 * mm, "dy" : 0 * mm, "dz" : getVariable(context, 'Hoogtedak') - getVariable(context, 'Dikte') - 10 * mm, "makeCopy" : true});
        }
        {
            var Q0;
            Q0=makeQuery(id+"F12.opExtrude","SWEPT_BODY",BODY,{"disambiguationData":[OSD([sQuery(id+"F4.wireOp",EDGE,"E27.bottom"),sQuery(id+"F4.wireOp",EDGE,"E27.top"),sQuery(id+"F4.wireOp",EDGE,"E27.left"),sQuery(id+"F4.wireOp",EDGE,"E27.right")])]});
            var Q1;
            Q1=makeQuery(id+"F12.opExtrude","CAP_VERTEX",VERTEX,{"disambiguationData":[OSD([sQuery(id+"F4.wireOp",EDGE,"E27.bottom"),sQuery(id+"F4.wireOp",EDGE,"E27.left")])],"isStart":false});
            var Q2;
            Q2=makeQuery(id+"F12.opExtrude","CAP_VERTEX",VERTEX,{"disambiguationData":[OSD([sQuery(id+"F4.wireOp",EDGE,"E27.bottom"),sQuery(id+"F4.wireOp",EDGE,"E27.right")])],"isStart":false});
            transform(context, id + "F41", {"entities" : qUnion([Q0]), "transformType" : TransformType.TRANSLATION_ENTITY, "oppositeDirectionEntity" : false, "transformLine" : qUnion([Q1, Q2]), "makeCopy" : true});
        }
        {
            var Q0;
            Q0=makeQuery(id+"F12.opExtrude","SWEPT_BODY",BODY,{"disambiguationData":[OSD([sQuery(id+"F4.wireOp",EDGE,"E23.bottom"),sQuery(id+"F4.wireOp",EDGE,"E23.top"),sQuery(id+"F4.wireOp",EDGE,"E23.left"),sQuery(id+"F4.wireOp",EDGE,"E23.right")])]});
            var Q1;
            Q1=makeQuery(id+"F12.opExtrude","CAP_VERTEX",VERTEX,{"disambiguationData":[OSD([sQuery(id+"F4.wireOp",EDGE,"E23.bottom"),sQuery(id+"F4.wireOp",EDGE,"E23.right")])],"isStart":false});
            var Q2;
            Q2=makeQuery(id+"F12.opExtrude","CAP_VERTEX",VERTEX,{"disambiguationData":[OSD([sQuery(id+"F4.wireOp",EDGE,"E23.bottom"),sQuery(id+"F4.wireOp",EDGE,"E23.left")])],"isStart":false});
            transform(context, id + "F42", {"entities" : qUnion([Q0]), "transformType" : TransformType.TRANSLATION_ENTITY, "oppositeDirectionEntity" : false, "transformLine" : qUnion([Q1, Q2]), "makeCopy" : true});
        }
        {
            var Q0;
            Q0=makeQuery(id+"F7.opExtrude","CAP_FACE",FACE,{"disambiguationData":[OSD([sQuery(id+"F6.wireOp",EDGE,"E30.bottom"),sQuery(id+"F6.wireOp",EDGE,"E30.top"),sQuery(id+"F6.wireOp",EDGE,"E30.left"),sQuery(id+"F6.wireOp",EDGE,"E30.right")])],"isStart":true});
            var sketch = newSketch(context, id + "F43", { "sketchPlane" : qUnion([Q0])});
            skLineSegment(sketch, "E85.bottom", {"start": v(-144, 58) * mm, "end": v(132.92, 58) * mm});
            skLineSegment(sketch, "E85.top", {"start": v(-144, 54) * mm, "end": v(132.92, 54) * mm});
            skLineSegment(sketch, "E85.left", {"start": v(-144, 58) * mm, "end": v(-144, 54) * mm});
            skLineSegment(sketch, "E85.right", {"start": v(132.92, 58) * mm, "end": v(132.92, 54) * mm});
            skLineSegment(sketch, "E86.bottom", {"start": v(-144, -140) * mm, "end": v(132.92, -140) * mm});
            skLineSegment(sketch, "E86.top", {"start": v(-144, -144) * mm, "end": v(132.92, -144) * mm});
            skLineSegment(sketch, "E86.left", {"start": v(-144, -140) * mm, "end": v(-144, -144) * mm});
            skLineSegment(sketch, "E86.right", {"start": v(132.92, -140) * mm, "end": v(132.92, -144) * mm});
            skSolve(sketch);
        }
        {
            var Q0;
            Q0 = qSketchRegion(id + "F43", true);
            extrude(context, id + "F44", {"entities" : qUnion([Q0]), "depth" : 10 * mm + getVariable(context, 'Dikte'), "offsetDistance" : 25 * mm});
        }
        {
            var Q0;
            Q0=makeQuery(id+"F9.opExtrude","CAP_FACE",FACE,{"disambiguationData":[OSD([sQuery(id+"F8.wireOp",EDGE,"E31.bottom"),sQuery(id+"F8.wireOp",EDGE,"E31.top"),sQuery(id+"F8.wireOp",EDGE,"E31.left"),sQuery(id+"F8.wireOp",EDGE,"E31.right")])],"isStart":true});
            var sketch = newSketch(context, id + "F45", { "sketchPlane" : qUnion([Q0])});
            skLineSegment(sketch, "E87.bottom", {"start": v(-148, 58) * mm, "end": v(-144, 58) * mm});
            skLineSegment(sketch, "E87.top", {"start": v(-148, -144) * mm, "end": v(-144, -144) * mm});
            skLineSegment(sketch, "E87.left", {"start": v(-148, 58) * mm, "end": v(-148, -144) * mm});
            skLineSegment(sketch, "E87.right", {"start": v(-144, 58) * mm, "end": v(-144, -144) * mm});
            skLineSegment(sketch, "E88.bottom", {"start": v(136.92, -144) * mm, "end": v(132.92, -144) * mm});
            skLineSegment(sketch, "E88.top", {"start": v(136.92, 58) * mm, "end": v(132.92, 58) * mm});
            skLineSegment(sketch, "E88.left", {"start": v(136.92, -144) * mm, "end": v(136.92, 58) * mm});
            skLineSegment(sketch, "E88.right", {"start": v(132.92, -144) * mm, "end": v(132.92, 58) * mm});
            skSolve(sketch);
        }
        {
            var Q0;
            Q0 = qSketchRegion(id + "F45", true);
            extrude(context, id + "F46", {"entities" : qUnion([Q0]), "depth" : 10 * mm + getVariable(context, 'Dikte'), "offsetDistance" : 25 * mm});
        }
        {
            var Q0;
            Q0=makeQuery(id+"F9.opExtrude","SWEPT_BODY",BODY,{"disambiguationData":[OSD([sQuery(id+"F8.wireOp",EDGE,"E33.bottom"),sQuery(id+"F8.wireOp",EDGE,"E33.top"),sQuery(id+"F8.wireOp",EDGE,"E33.left"),sQuery(id+"F8.wireOp",EDGE,"E33.right")])]});
            var Q1;
            Q1=makeQuery(id+"F7.opExtrude","SWEPT_BODY",BODY,{"disambiguationData":[OSD([sQuery(id+"F6.wireOp",EDGE,"E30.bottom"),sQuery(id+"F6.wireOp",EDGE,"E30.top"),sQuery(id+"F6.wireOp",EDGE,"E30.left"),sQuery(id+"F6.wireOp",EDGE,"E30.right")])]});
            var Q2;
            Q2=makeQuery(id+"F7.opExtrude","SWEPT_BODY",BODY,{"disambiguationData":[OSD([sQuery(id+"F6.wireOp",EDGE,"E28.bottom"),sQuery(id+"F6.wireOp",EDGE,"E28.top"),sQuery(id+"F6.wireOp",EDGE,"E28.left"),sQuery(id+"F6.wireOp",EDGE,"E28.right")])]});
            var Q3;
            Q3=makeQuery(id+"F9.opExtrude","SWEPT_BODY",BODY,{"disambiguationData":[OSD([sQuery(id+"F8.wireOp",EDGE,"E31.bottom"),sQuery(id+"F8.wireOp",EDGE,"E31.top"),sQuery(id+"F8.wireOp",EDGE,"E31.left"),sQuery(id+"F8.wireOp",EDGE,"E31.right")])]});
            var Q4;
            Q4=makeQuery(id+"F11.opExtrude","SWEPT_BODY",BODY,{"disambiguationData":[OSD([sQuery(id+"F10.wireOp",EDGE,"E34.bottom"),sQuery(id+"F10.wireOp",EDGE,"E34.top"),sQuery(id+"F10.wireOp",EDGE,"E34.left"),sQuery(id+"F10.wireOp",EDGE,"E34.right")])]});
            booleanBodies(context, id + "F47", {"operationType" : BooleanOperationType.SUBTRACTION, "tools" : qUnion([Q0, Q1, Q2, Q3]), "targets" : qUnion([Q4]), "keepTools" : true});
        }
    });
